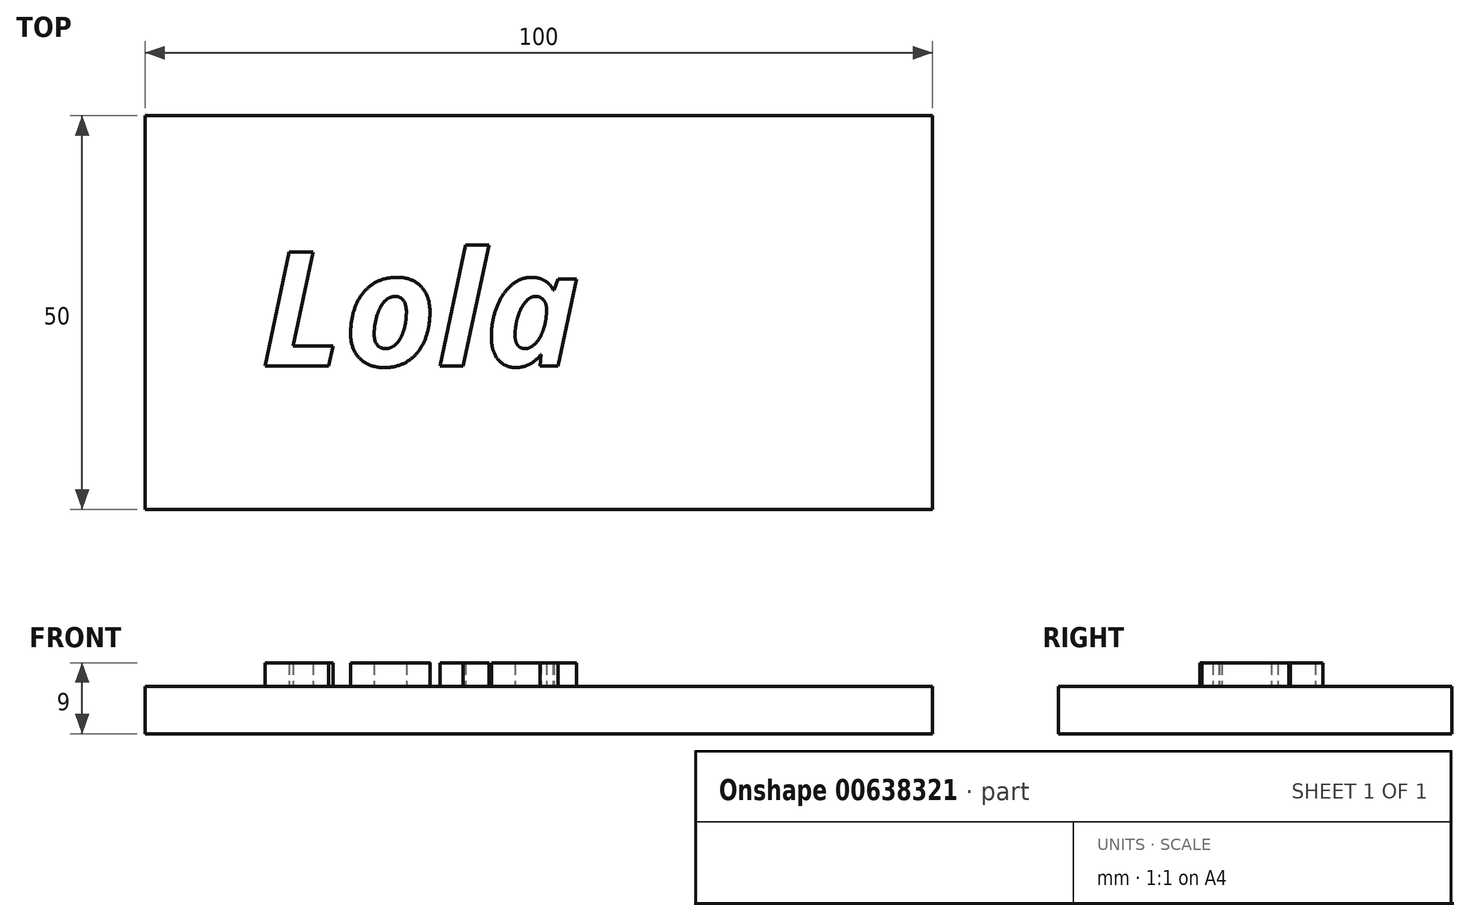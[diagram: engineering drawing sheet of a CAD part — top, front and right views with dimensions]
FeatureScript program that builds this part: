
annotation { "Feature Type Name" : "Feature", "Feature Type Description" : "" }
export const myFeature = defineFeature(function(context is Context, id is Id, definition is map)
    precondition{}
    {
        {
            var Q0;
            Q0=qCreatedBy(makeId("Top.planeOp"),FACE);
            var sketch = newSketch(context, id + "F0", { "sketchPlane" : qUnion([Q0])});
            skLineSegment(sketch, "E0.bottom", {"start": v(0, 0) * mm, "end": v(-100, 0) * mm});
            skLineSegment(sketch, "E0.top", {"start": v(0, 50) * mm, "end": v(-100, 50) * mm});
            skLineSegment(sketch, "E0.left", {"start": v(0, 0) * mm, "end": v(0, 50) * mm});
            skLineSegment(sketch, "E0.right", {"start": v(-100, 0) * mm, "end": v(-100, 50) * mm});
            skSolve(sketch);
        }
        {
            var Q0;
            Q0 = qSketchRegion(id + "F0", true);
            extrude(context, id + "F1", {"entities" : qUnion([Q0]), "depth" : 3 * mm, "offsetDistance" : 25 * mm});
        }
        {
            var Q0;
            Q0=makeQuery(id+"F1.opExtrude","CAP_FACE",FACE,{"disambiguationData":[OSD([sQuery(id+"F0.wireOp",EDGE,"E0.bottom"),sQuery(id+"F0.wireOp",EDGE,"E0.top"),sQuery(id+"F0.wireOp",EDGE,"E0.left"),sQuery(id+"F0.wireOp",EDGE,"E0.right")])],"isStart":false});
            var Q1;
            Q1 = qSketchRegion(id + "FJI3pt9l65Sn1QI_1", true);
            extrude(context, id + "F2", {"entities" : qUnion([Q0, Q1]), "operationType" : NewBodyOperationType.ADD, "depth" : 3 * mm, "offsetDistance" : 25 * mm});
        }
        {
            var Q0;
            Q0=makeQuery(id+"F2.opExtrude","CAP_FACE",FACE,{"disambiguationData":[OSD([sQuery(id+"F0.wireOp",EDGE,"E0.bottom"),sQuery(id+"F0.wireOp",EDGE,"E0.top"),sQuery(id+"F0.wireOp",EDGE,"E0.left"),sQuery(id+"F0.wireOp",EDGE,"E0.right")])],"isStart":false});
            var sketch = newSketch(context, id + "F3", { "sketchPlane" : qUnion([Q0])});
            skText(sketch, "E1", { "text": "Lola", "fontName": "OpenSans-BoldItalic.ttf"});
            const initialGuessF3  = {"E1": [-0.08529, 0.01821, 1, 0, 0.01459]};
            skSetInitialGuess(sketch, initialGuessF3);
            skSolve(sketch);
        }
        {
            var Q0;
            Q0 = qSketchRegion(id + "F3", true);
            extrude(context, id + "F4", {"entities" : qUnion([Q0]), "operationType" : NewBodyOperationType.ADD, "depth" : 3 * mm, "offsetDistance" : 25 * mm});
        }
    });
